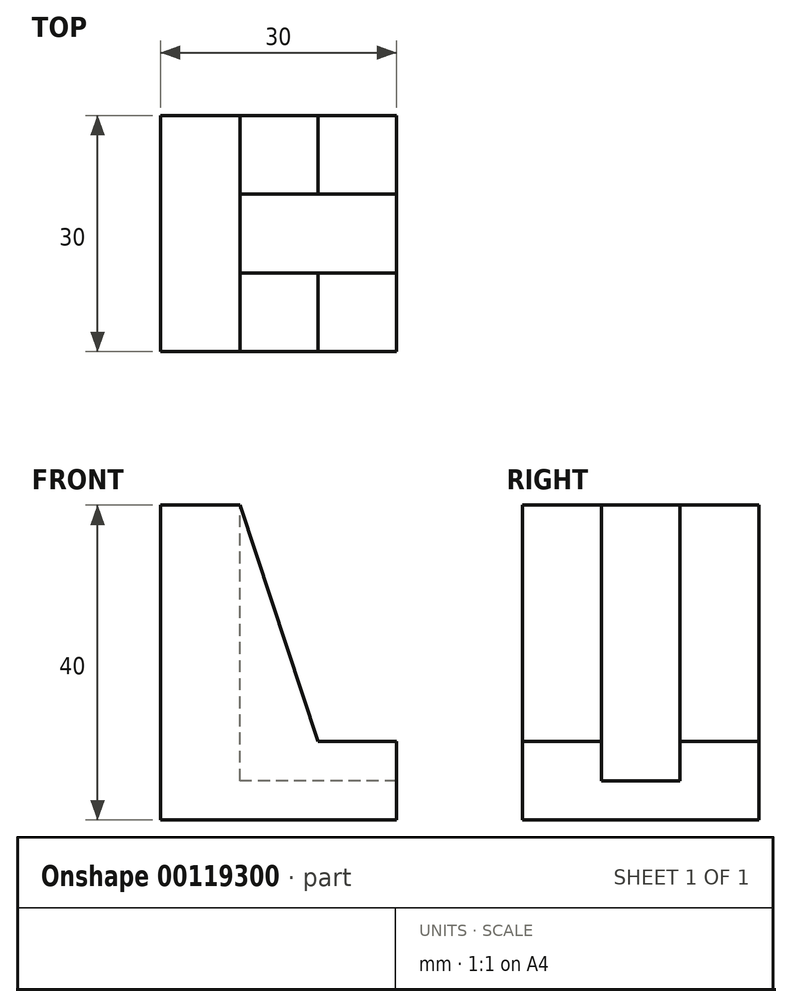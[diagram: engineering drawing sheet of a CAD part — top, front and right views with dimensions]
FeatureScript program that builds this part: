
annotation { "Feature Type Name" : "Feature", "Feature Type Description" : "" }
export const myFeature = defineFeature(function(context is Context, id is Id, definition is map)
    precondition{}
    {
        {
            var Q0;
            Q0=qCreatedBy(makeId("Front.planeOp"),FACE);
            var sketch = newSketch(context, id + "F0", { "sketchPlane" : qUnion([Q0])});
            skLineSegment(sketch, "E0", {"start": v(0, 40) * mm, "end": v(10.1, 40) * mm});
            skLineSegment(sketch, "E1", {"start": v(10.1, 40) * mm, "end": v(20, 10) * mm});
            skLineSegment(sketch, "E2", {"start": v(20, 10) * mm, "end": v(30, 10) * mm});
            skLineSegment(sketch, "E3", {"start": v(30, 10) * mm, "end": v(30, 0) * mm});
            skLineSegment(sketch, "E4", {"start": v(30, 0) * mm, "end": v(0, 0) * mm});
            skLineSegment(sketch, "E5", {"start": v(0, 0) * mm, "end": v(0, 40) * mm});
            skSolve(sketch);
        }
        {
            var Q0;
            Q0=makeQuery(id+"F0.imprint","IMPRINT",FACE,{"disambiguationData":[TD([[makeQuery(id+"F0.imprint","IMPRINT",EDGE,{"derivedFrom":sQuery(id+"F0.wireOp",EDGE,"E0")}),-1.0]])]});
            extrude(context, id + "F1", {"entities" : qUnion([Q0]), "depth" : 30 * mm});
        }
        {
            var Q0;
            Q0=makeQuery(id+"F1.opExtrude","SWEPT_FACE",FACE,{"disambiguationData":[OSD([sQuery(id+"F0.wireOp",EDGE,"E0")])]});
            var sketch = newSketch(context, id + "F2", { "sketchPlane" : qUnion([Q0])});
            skLineSegment(sketch, "E6.bottom", {"start": v(54.53, -10) * mm, "end": v(10.1, -10) * mm});
            skLineSegment(sketch, "E6.top", {"start": v(54.53, -20) * mm, "end": v(10.1, -20) * mm});
            skLineSegment(sketch, "E6.left", {"start": v(54.53, -10) * mm, "end": v(54.53, -20) * mm});
            skLineSegment(sketch, "E6.right", {"start": v(10.1, -10) * mm, "end": v(10.1, -20) * mm});
            skSolve(sketch);
        }
        {
            var Q0;
            Q0 = qSketchRegion(id + "F2", true);
            extrude(context, id + "F3", {"entities" : qUnion([Q0]), "operationType" : NewBodyOperationType.REMOVE, "oppositeDirection" : true, "depth" : 35 * mm});
        }
    });
